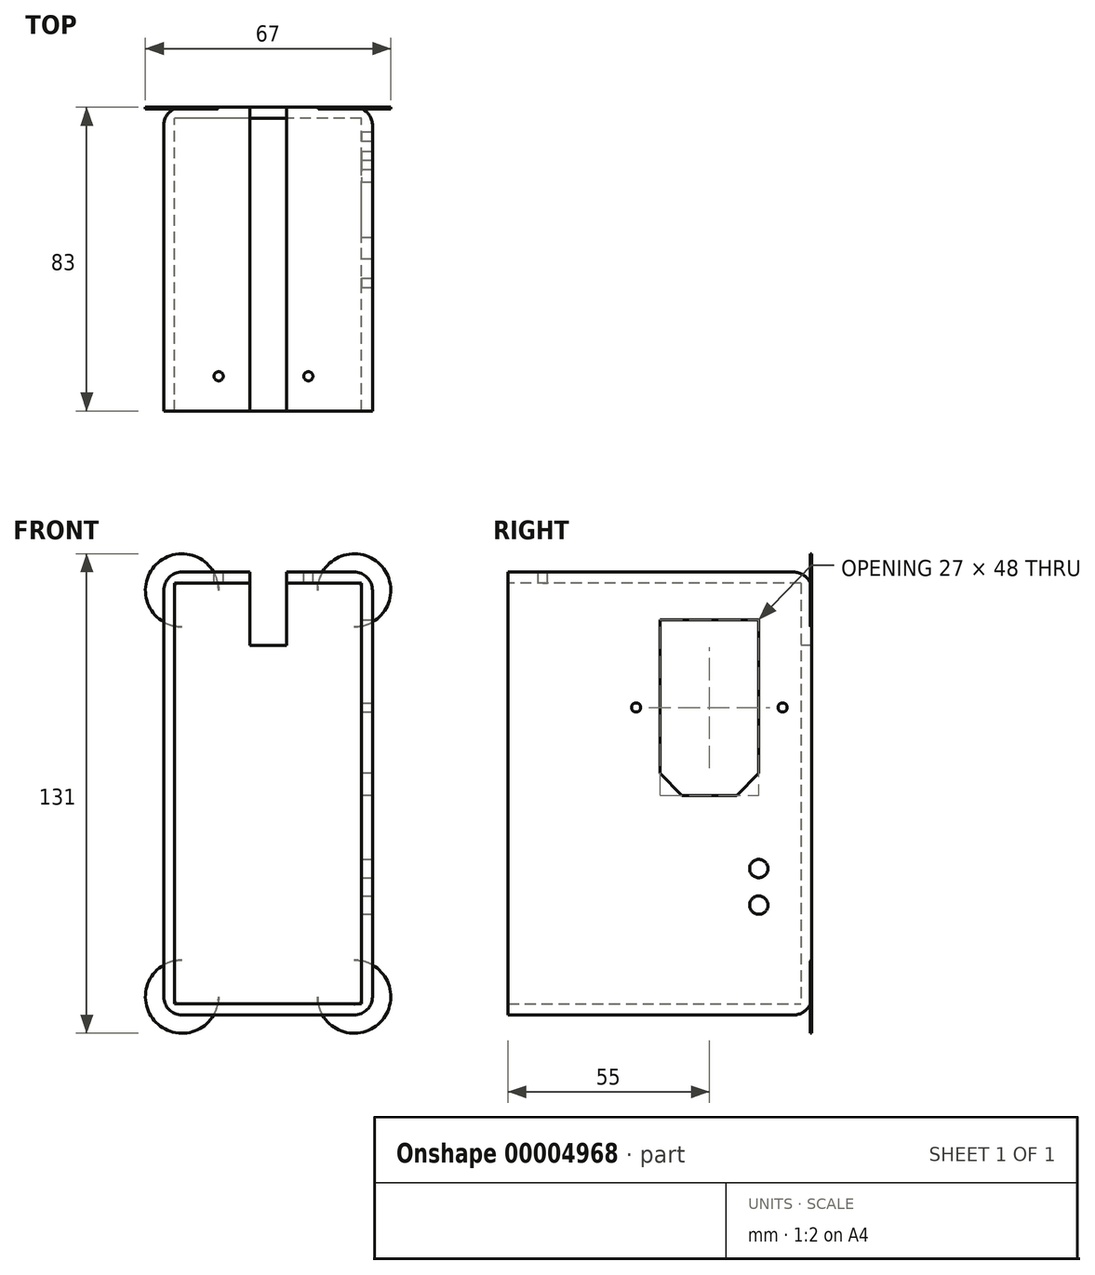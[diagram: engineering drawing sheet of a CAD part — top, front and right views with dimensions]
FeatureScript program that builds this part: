
annotation { "Feature Type Name" : "Feature", "Feature Type Description" : "" }
export const myFeature = defineFeature(function(context is Context, id is Id, definition is map)
    precondition{}
    {
        {
            var Q0;
            Q0=qCreatedBy(makeId("Front.planeOp"),FACE);
            var sketch = newSketch(context, id + "F0", { "sketchPlane" : qUnion([Q0])});
            skLineSegment(sketch, "E0.rect.bottom", {"start": v(25.5, 57.5) * mm, "end": v(-25.5, 57.5) * mm});
            skLineSegment(sketch, "E0.rect.top", {"start": v(25.5, -57.5) * mm, "end": v(-25.5, -57.5) * mm});
            skLineSegment(sketch, "E0.rect.left", {"start": v(25.5, 57.5) * mm, "end": v(25.5, -57.5) * mm});
            skLineSegment(sketch, "E0.rect.right", {"start": v(-25.5, 57.5) * mm, "end": v(-25.5, -57.5) * mm});
            skPoint(sketch, "E0.rect.middle", {"position": v(0, 0) * mm});
            skLineSegment(sketch, "E1.rect.bottom", {"start": v(28.5, 60.5) * mm, "end": v(-28.5, 60.5) * mm});
            skLineSegment(sketch, "E1.rect.top", {"start": v(28.5, -60.5) * mm, "end": v(-28.5, -60.5) * mm});
            skLineSegment(sketch, "E1.rect.left", {"start": v(28.5, 60.5) * mm, "end": v(28.5, -60.5) * mm});
            skLineSegment(sketch, "E1.rect.right", {"start": v(-28.5, 60.5) * mm, "end": v(-28.5, -60.5) * mm});
            skSolve(sketch);
        }
        {
            var Q0;
            Q0 = qSketchRegion(id + "F0", true);
            extrude(context, id + "F1", {"entities" : qUnion([Q0]), "depth" : 80 * mm, "symmetric" : true});
        }
        {
            var Q0;
            Q0=makeQuery(id+"F1.opExtrude","CAP_FACE",FACE,{"disambiguationData":[OSD([sQuery(id+"F0.wireOp",EDGE,"E0.rect.bottom"),sQuery(id+"F0.wireOp",EDGE,"E0.rect.top"),sQuery(id+"F0.wireOp",EDGE,"E0.rect.left"),sQuery(id+"F0.wireOp",EDGE,"E0.rect.right"),sQuery(id+"F0.wireOp",EDGE,"E1.rect.bottom"),sQuery(id+"F0.wireOp",EDGE,"E1.rect.top"),sQuery(id+"F0.wireOp",EDGE,"E1.rect.left"),sQuery(id+"F0.wireOp",EDGE,"E1.rect.right")])],"isStart":false});
            var sketch = newSketch(context, id + "F2", { "sketchPlane" : qUnion([Q0])});
            skLineSegment(sketch, "E2", {"start": v(0, 60.5) * mm, "end": v(0, -57.5) * mm, "construction": true});
            skLineSegment(sketch, "E3.bottom", {"start": v(-5, 60.5) * mm, "end": v(5, 60.5) * mm});
            skLineSegment(sketch, "E3.top", {"start": v(-5, 57.5) * mm, "end": v(5, 57.5) * mm});
            skLineSegment(sketch, "E3.left", {"start": v(-5, 60.5) * mm, "end": v(-5, 57.5) * mm});
            skLineSegment(sketch, "E3.right", {"start": v(5, 60.5) * mm, "end": v(5, 57.5) * mm});
            skSolve(sketch);
        }
        {
            var Q0;
            Q0 = qSketchRegion(id + "F2", true);
            extrude(context, id + "F3", {"entities" : qUnion([Q0]), "operationType" : NewBodyOperationType.REMOVE, "endBound" : BoundingType.THROUGH_ALL, "oppositeDirection" : true, "depth" : 25 * mm});
        }
        {
            var Q0;
            Q0=makeQuery(id+"F1.opExtrude","CAP_FACE",FACE,{"disambiguationData":[OSD([sQuery(id+"F0.wireOp",EDGE,"E0.rect.bottom"),sQuery(id+"F0.wireOp",EDGE,"E0.rect.top"),sQuery(id+"F0.wireOp",EDGE,"E0.rect.left"),sQuery(id+"F0.wireOp",EDGE,"E0.rect.right"),sQuery(id+"F0.wireOp",EDGE,"E1.rect.bottom"),sQuery(id+"F0.wireOp",EDGE,"E1.rect.top"),sQuery(id+"F0.wireOp",EDGE,"E1.rect.left"),sQuery(id+"F0.wireOp",EDGE,"E1.rect.right")])],"isStart":true});
            var sketch = newSketch(context, id + "F4", { "sketchPlane" : qUnion([Q0])});
            skLineSegment(sketch, "E4.bottom", {"start": v(-28.5, 60.5) * mm, "end": v(28.5, 60.5) * mm, "construction": true});
            skLineSegment(sketch, "E4.top", {"start": v(-28.5, -60.5) * mm, "end": v(28.5, -60.5) * mm});
            skLineSegment(sketch, "E4.left", {"start": v(-28.5, 60.5) * mm, "end": v(-28.5, -60.5) * mm});
            skLineSegment(sketch, "E4.right", {"start": v(28.5, 60.5) * mm, "end": v(28.5, -60.5) * mm});
            skLineSegment(sketch, "E5", {"start": v(-28.5, 60.5) * mm, "end": v(-5, 60.5) * mm});
            skLineSegment(sketch, "E6", {"start": v(-5, 60.5) * mm, "end": v(-5, 40.5) * mm});
            skLineSegment(sketch, "E7", {"start": v(-5, 40.5) * mm, "end": v(5, 40.5) * mm});
            skLineSegment(sketch, "E8", {"start": v(5, 40.5) * mm, "end": v(5, 60.5) * mm});
            skLineSegment(sketch, "E9", {"start": v(5, 60.5) * mm, "end": v(28.5, 60.5) * mm});
            skSolve(sketch);
        }
        {
            var Q0;
            Q0 = qSketchRegion(id + "F4", true);
            extrude(context, id + "F5", {"entities" : qUnion([Q0]), "operationType" : NewBodyOperationType.ADD, "depth" : 3 * mm});
        }
        {
            var Q0;
            Q0=makeQuery(id+"F5.boolean.opBoolean","MERGE",FACE,{"derivedFrom":[makeQuery(id+"F1.opExtrude","SWEPT_FACE",FACE,{"disambiguationData":[OSD([sQuery(id+"F0.wireOp",EDGE,"E1.rect.left")])]}),makeQuery(id+"F5.opExtrude","SWEPT_FACE",FACE,{"disambiguationData":[OSD([sQuery(id+"F4.wireOp",EDGE,"E4.left")])]})]});
            var sketch = newSketch(context, id + "F6", { "sketchPlane" : qUnion([Q0])});
            skLineSegment(sketch, "E10.0", {"start": v(40, 57.5) * mm, "end": v(40, -57.5) * mm, "construction": true});
            skLineSegment(sketch, "E11", {"start": v(-10, 35.01) * mm, "end": v(-10, -35.01) * mm, "construction": true});
            skLineSegment(sketch, "E12", {"start": v(-10, 0) * mm, "end": v(40, 0) * mm, "construction": true});
            skLineSegment(sketch, "E13", {"start": v(15, 0) * mm, "end": v(15, 77.3) * mm, "construction": true});
            skCircle(sketch, "E14", {"center": v(-5, 23.5) * mm, "radius": 1.25 * mm});
            skCircle(sketch, "E15.MirrorC", {"center": v(35, 23.5) * mm, "radius": 1.25 * mm});
            skLineSegment(sketch, "E16", {"start": v(-5, 23.5) * mm, "end": v(35, 23.5) * mm, "construction": true});
            skLineSegment(sketch, "E17.rect.bottom", {"start": v(28.5, 47.5) * mm, "end": v(1.5, 47.5) * mm});
            skLineSegment(sketch, "E17.rect.top", {"start": v(28.5, -0.5) * mm, "end": v(1.5, -0.5) * mm});
            skLineSegment(sketch, "E17.rect.left", {"start": v(28.5, 47.5) * mm, "end": v(28.5, -0.5) * mm});
            skLineSegment(sketch, "E17.rect.right", {"start": v(1.5, 47.5) * mm, "end": v(1.5, -0.5) * mm});
            skPoint(sketch, "E17.rect.middle", {"position": v(15, 23.5) * mm});
            skLineSegment(sketch, "E18.0", {"start": v(-40, 57.5) * mm, "end": v(40, 57.5) * mm, "construction": true});
            skLineSegment(sketch, "E19", {"start": v(28.5, -0.5) * mm, "end": v(28.5, -51.13) * mm, "construction": true});
            skCircle(sketch, "E20", {"center": v(28.5, -20.5) * mm, "radius": 2.5 * mm});
            skCircle(sketch, "E21", {"center": v(28.5, -30.5) * mm, "radius": 2.5 * mm});
            skSolve(sketch);
        }
        {
            var Q0;
            Q0 = qSketchRegion(id + "F6", true);
            var Q1;
            Q1=makeQuery(id+"F1.opExtrude","SWEPT_FACE",FACE,{"disambiguationData":[OSD([sQuery(id+"F0.wireOp",EDGE,"E0.rect.left")])]});
            extrude(context, id + "F7", {"entities" : qUnion([Q0]), "operationType" : NewBodyOperationType.REMOVE, "endBound" : BoundingType.UP_TO_SURFACE, "oppositeDirection" : true, "endBoundEntityFace" : qUnion([Q1]), "depth" : 25 * mm});
        }
        {
            var Q0;
            Q0=makeQuery(id+"F7.boolean.opBoolean","COPY",EDGE,{"derivedFrom":makeQuery(id+"F7.opExtrude","SWEPT_EDGE",EDGE,{"disambiguationData":[OSD([sQuery(id+"F6.wireOp",EDGE,"E17.rect.top"),sQuery(id+"F6.wireOp",EDGE,"E17.rect.left")])]})});
            var Q1;
            Q1=makeQuery(id+"F7.boolean.opBoolean","COPY",EDGE,{"derivedFrom":makeQuery(id+"F7.opExtrude","SWEPT_EDGE",EDGE,{"disambiguationData":[OSD([sQuery(id+"F6.wireOp",EDGE,"E17.rect.top"),sQuery(id+"F6.wireOp",EDGE,"E17.rect.right")])]})});
            chamfer(context, id + "F8", {"entities" : qUnion([Q0, Q1]), "width" : 6 * mm, "tangentPropagation" : true});
        }
        {
            var Q0;
            Q0=makeQuery(id+"F3.boolean.opBoolean","COPY",EDGE,{"derivedFrom":makeQuery(id+"F3.opExtrude","CAP_EDGE",EDGE,{"disambiguationData":[OSD([sQuery(id+"F2.wireOp",EDGE,"E3.left")])],"isStart":true})});
            var Q1;
            Q1=makeQuery(id+"F3.boolean.opBoolean","COPY",EDGE,{"derivedFrom":makeQuery(id+"F3.opExtrude","CAP_EDGE",EDGE,{"disambiguationData":[OSD([sQuery(id+"F2.wireOp",EDGE,"E3.right")])],"isStart":true})});
            var Q2;
            Q2=makeQuery(id+"F5.opExtrude","CAP_EDGE",EDGE,{"disambiguationData":[OSD([sQuery(id+"F4.wireOp",EDGE,"E5")])],"isStart":false});
            var Q3;
            Q3=makeQuery(id+"F5.opExtrude","CAP_EDGE",EDGE,{"disambiguationData":[OSD([sQuery(id+"F4.wireOp",EDGE,"E9")])],"isStart":false});
            var Q4;
            Q4=makeQuery(id+"F5.opExtrude","CAP_EDGE",EDGE,{"disambiguationData":[OSD([sQuery(id+"F4.wireOp",EDGE,"E4.top")])],"isStart":false});
            var Q5;
            Q5=makeQuery(id+"F5.boolean.opBoolean","MERGE",EDGE,{"derivedFrom":[makeQuery(id+"F1.opExtrude","SWEPT_EDGE",EDGE,{"disambiguationData":[OSD([sQuery(id+"F0.wireOp",EDGE,"E1.rect.top"),sQuery(id+"F0.wireOp",EDGE,"E1.rect.left")])]}),makeQuery(id+"F5.opExtrude","SWEPT_EDGE",EDGE,{"disambiguationData":[OSD([sQuery(id+"F4.wireOp",EDGE,"E4.top"),sQuery(id+"F4.wireOp",EDGE,"E4.left")])]})]});
            var Q6;
            Q6=makeQuery(id+"F5.boolean.opBoolean","MERGE",EDGE,{"derivedFrom":[makeQuery(id+"F1.opExtrude","SWEPT_EDGE",EDGE,{"disambiguationData":[OSD([sQuery(id+"F0.wireOp",EDGE,"E1.rect.top"),sQuery(id+"F0.wireOp",EDGE,"E1.rect.right")])]}),makeQuery(id+"F5.opExtrude","SWEPT_EDGE",EDGE,{"disambiguationData":[OSD([sQuery(id+"F4.wireOp",EDGE,"E4.top"),sQuery(id+"F4.wireOp",EDGE,"E4.right")])]})]});
            var Q7;
            Q7=makeQuery(id+"F5.boolean.opBoolean","MERGE",EDGE,{"derivedFrom":[makeQuery(id+"F1.opExtrude","SWEPT_EDGE",EDGE,{"disambiguationData":[OSD([sQuery(id+"F0.wireOp",EDGE,"E1.rect.bottom"),sQuery(id+"F0.wireOp",EDGE,"E1.rect.right")])]}),makeQuery(id+"F5.opExtrude","SWEPT_EDGE",EDGE,{"disambiguationData":[OSD([sQuery(id+"F4.wireOp",EDGE,"E4.right"),sQuery(id+"F4.wireOp",EDGE,"E9")])]})]});
            var Q8;
            Q8=makeQuery(id+"F5.boolean.opBoolean","MERGE",EDGE,{"derivedFrom":[makeQuery(id+"F1.opExtrude","SWEPT_EDGE",EDGE,{"disambiguationData":[OSD([sQuery(id+"F0.wireOp",EDGE,"E1.rect.bottom"),sQuery(id+"F0.wireOp",EDGE,"E1.rect.left")])]}),makeQuery(id+"F5.opExtrude","SWEPT_EDGE",EDGE,{"disambiguationData":[OSD([sQuery(id+"F4.wireOp",EDGE,"E4.left"),sQuery(id+"F4.wireOp",EDGE,"E5")])]})]});
            var Q9;
            Q9=makeQuery(id+"F5.opExtrude","CAP_EDGE",EDGE,{"disambiguationData":[OSD([sQuery(id+"F4.wireOp",EDGE,"E4.left")])],"isStart":false});
            var Q10;
            Q10=makeQuery(id+"F5.opExtrude","CAP_EDGE",EDGE,{"disambiguationData":[OSD([sQuery(id+"F4.wireOp",EDGE,"E4.right")])],"isStart":false});
            fillet(context, id + "F9", {"entities" : qUnion([Q0, Q1, Q2, Q3, Q4, Q5, Q6, Q7, Q8, Q9, Q10]), "radius" : 5 * mm, "tangentPropagation" : true, "allowEdgeOverflow" : false});
        }
        {
            var Q0;
            {var subQ0=sQuery(id+"F0.wireOp",EDGE,"E1.rect.bottom");var subQ1=sQuery(id+"F0.wireOp",EDGE,"E1.rect.right");Q0=makeQuery(id+"F5.boolean.opBoolean","MERGE",FACE,{"derivedFrom":[makeQuery(id+"F3.boolean.opBoolean","SPLIT",FACE,{"disambiguationData":[TD([makeQuery(id+"F1.opExtrude","SWEPT_FACE",FACE,{"disambiguationData":[OSD([subQ1])]})])],"derivedFrom":makeQuery(id+"F1.opExtrude","SWEPT_FACE",FACE,{"disambiguationData":[OSD([subQ0])]})}),makeQuery(id+"F5.opExtrude","SWEPT_FACE",FACE,{"disambiguationData":[OSD([sQuery(id+"F4.wireOp",EDGE,"E9")])]})]});}
            var sketch = newSketch(context, id + "F10", { "sketchPlane" : qUnion([Q0])});
            skLineSegment(sketch, "E22", {"start": v(-13.5, -30.5) * mm, "end": v(11, -30.5) * mm, "construction": true});
            skLineSegment(sketch, "E23.0", {"start": v(28.5, 28.5) * mm, "end": v(28.5, 1.5) * mm, "construction": true});
            skLineSegment(sketch, "E24.0", {"start": v(25.5, -40) * mm, "end": v(25.5, 40) * mm, "construction": true});
            skCircle(sketch, "E25", {"center": v(-13.5, -30.5) * mm, "radius": 1.25 * mm});
            skCircle(sketch, "E26", {"center": v(11, -30.5) * mm, "radius": 1.25 * mm});
            skSolve(sketch);
        }
        {
            var Q0;
            Q0 = qSketchRegion(id + "F10", true);
            extrude(context, id + "F11", {"entities" : qUnion([Q0]), "operationType" : NewBodyOperationType.REMOVE, "endBound" : BoundingType.UP_TO_NEXT, "oppositeDirection" : true, "depth" : 25 * mm});
        }
        {
            var Q0;
            Q0=makeQuery(id+"F5.opExtrude","CAP_FACE",FACE,{"disambiguationData":[OSD([sQuery(id+"F4.wireOp",EDGE,"E4.top"),sQuery(id+"F4.wireOp",EDGE,"E4.left"),sQuery(id+"F4.wireOp",EDGE,"E4.right"),sQuery(id+"F4.wireOp",EDGE,"E5"),sQuery(id+"F4.wireOp",EDGE,"E6"),sQuery(id+"F4.wireOp",EDGE,"E7"),sQuery(id+"F4.wireOp",EDGE,"E8"),sQuery(id+"F4.wireOp",EDGE,"E9")])],"isStart":false});
            var sketch = newSketch(context, id + "F12", { "sketchPlane" : qUnion([Q0])});
            skCircle(sketch, "E27", {"center": v(-23.5, -55.5) * mm, "radius": 10 * mm});
            skCircle(sketch, "E28", {"center": v(-23.5, 55.5) * mm, "radius": 10 * mm});
            skCircle(sketch, "E29", {"center": v(23.5, 55.5) * mm, "radius": 10 * mm});
            skCircle(sketch, "E30", {"center": v(23.5, -55.5) * mm, "radius": 10 * mm});
            skSolve(sketch);
        }
        {
            var Q0;
            Q0 = qSketchRegion(id + "F12", true);
            extrude(context, id + "F13", {"entities" : qUnion([Q0]), "operationType" : NewBodyOperationType.ADD, "oppositeDirection" : true, "depth" : 0.5 * mm});
        }
    });
